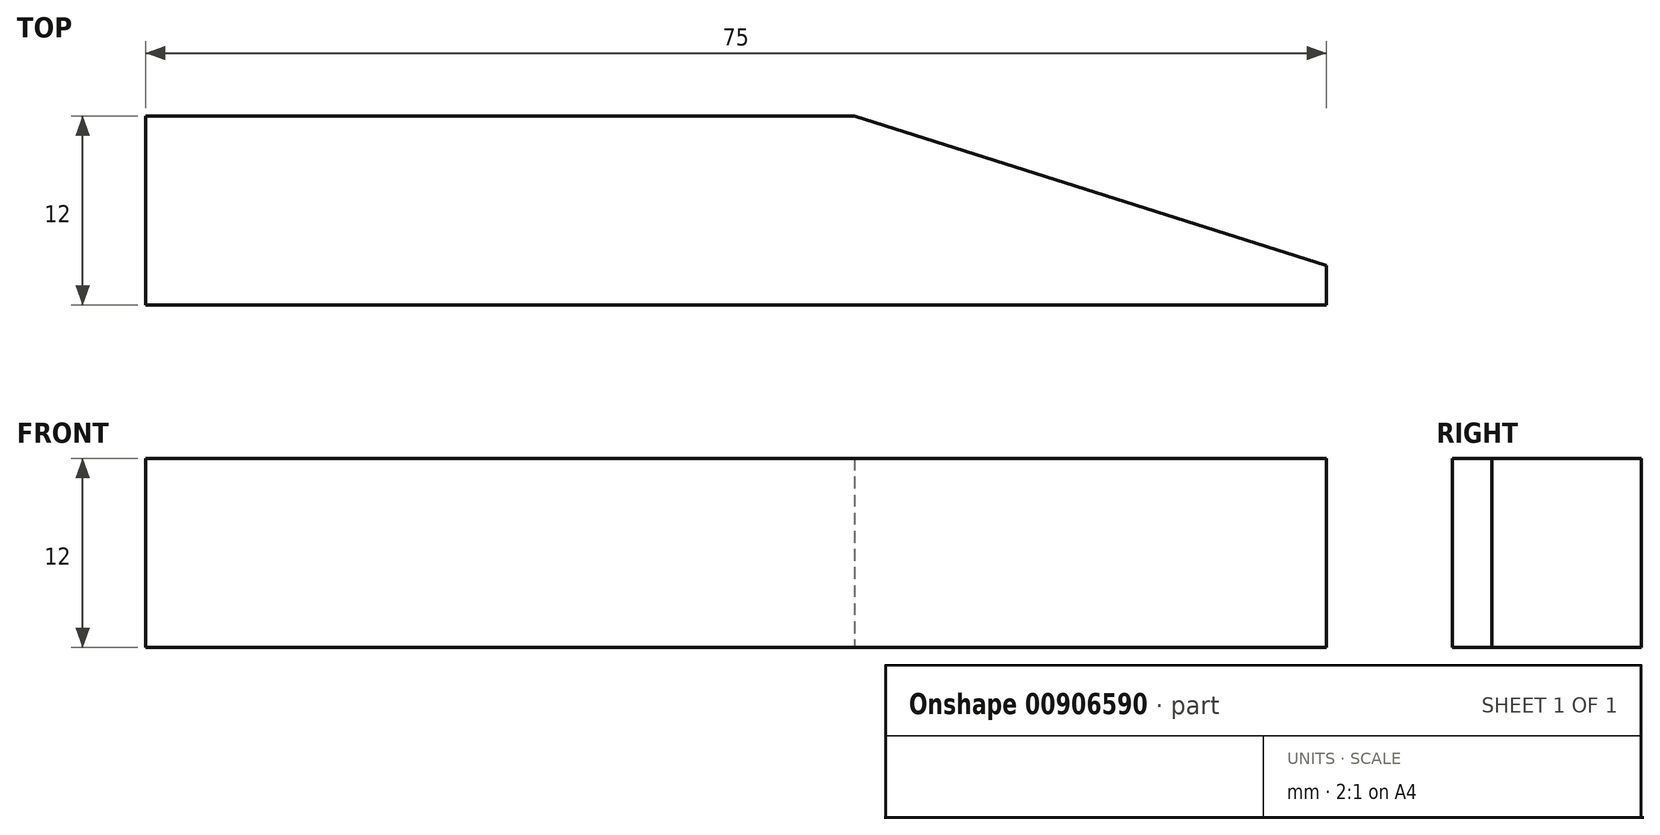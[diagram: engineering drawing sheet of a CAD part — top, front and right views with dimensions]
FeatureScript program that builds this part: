
annotation { "Feature Type Name" : "Feature", "Feature Type Description" : "" }
export const myFeature = defineFeature(function(context is Context, id is Id, definition is map)
    precondition{}
    {
        {
            var Q0;
            Q0=qCreatedBy(makeId("Top.planeOp"),FACE);
            var sketch = newSketch(context, id + "F0", { "sketchPlane" : qUnion([Q0])});
            skLineSegment(sketch, "E0", {"start": v(-21.67, 11.92) * mm, "end": v(23.33, 11.92) * mm});
            skLineSegment(sketch, "E1", {"start": v(23.33, 11.92) * mm, "end": v(53.33, 2.42) * mm});
            skLineSegment(sketch, "E2", {"start": v(53.33, 2.42) * mm, "end": v(53.33, -0.08) * mm});
            skLineSegment(sketch, "E3", {"start": v(53.33, -0.08) * mm, "end": v(-21.67, -0.08) * mm});
            skLineSegment(sketch, "E4", {"start": v(-21.67, -0.08) * mm, "end": v(-21.67, 11.92) * mm});
            skSolve(sketch);
        }
        {
            var Q0;
            Q0 = qSketchRegion(id + "F0", true);
            extrude(context, id + "F1", {"entities" : qUnion([Q0]), "depth" : 12 * mm, "offsetDistance" : 25 * mm});
        }
    });
